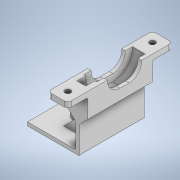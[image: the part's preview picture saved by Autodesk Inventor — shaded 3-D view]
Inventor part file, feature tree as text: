
AUTODESK INVENTOR PART (.ipt)
format: ipt  version: 2021 (Build 250183000, 183)  size: 319,488 bytes
history: native  units: mm
features: extrude x8, sketch x8, other x6, fillet x6, mirror x2, projected_geometry x2, shell x1, chamfer x1
ambient origin geometry x8: Origin, YZ Plane, XZ Plane, XY Plane, X Axis, Y Axis, Z Axis, Center Point
bodies: Body1 (feature_tree)
feature tree (34):
  other  "Твердое тело1"
  extrude  "Выдавливание1"  Depth=2.0mm
  extrude  "Выдавливание2"  Depth=20.0mm
  shell  "Оболочка1"  Thickness=2.0mm
  fillet  "Сопряжение1"  Radius=27.0mm
  fillet  "Сопряжение2"  Radius=26.1mm
  fillet  "Сопряжение3"  Radius=7.1mm
  chamfer  "Фаска1"  Distance=22.1mm
  other  "Непосредственное редактирование1"
  extrude  "Выдавливание8"  Depth=2.0mm
  extrude  "Выдавливание9"  Depth=2.0mm
  sketch  "Эскиз10"
  extrude  "Выдавливание10"  Depth=13.5mm TaperAngle=0.0deg
  extrude  "Выдавливание11"  Depth=2.0mm
  fillet  "Сопряжение6"  Radius=11.0mm
  extrude  "Выдавливание12"  Depth=1.0mm
  fillet  "Сопряжение7"  Radius=0.5mm
  fillet  "Сопряжение8"  Radius=4.55mm
  extrude  "Выдавливание13"  Depth=9.0mm
  other  "РабПлоскость2"
  other  "Ребро жесткости2"
  mirror  "Зеркальное отражение1"
  mirror  "Зеркальное отражение2"
  sketch  "Эскиз1"
  sketch  "Эскиз2"
  projected_geometry  "Спроецированная петля1"
  sketch  "Эскиз8"
  sketch  "Эскиз9"
  sketch  "Эскиз12"
  sketch  "Эскиз13"
  projected_geometry  "Спроецированная петля2"
  other  "РабПлоскость1"
  sketch  "Эскиз14"
  other  "Перенос1"
